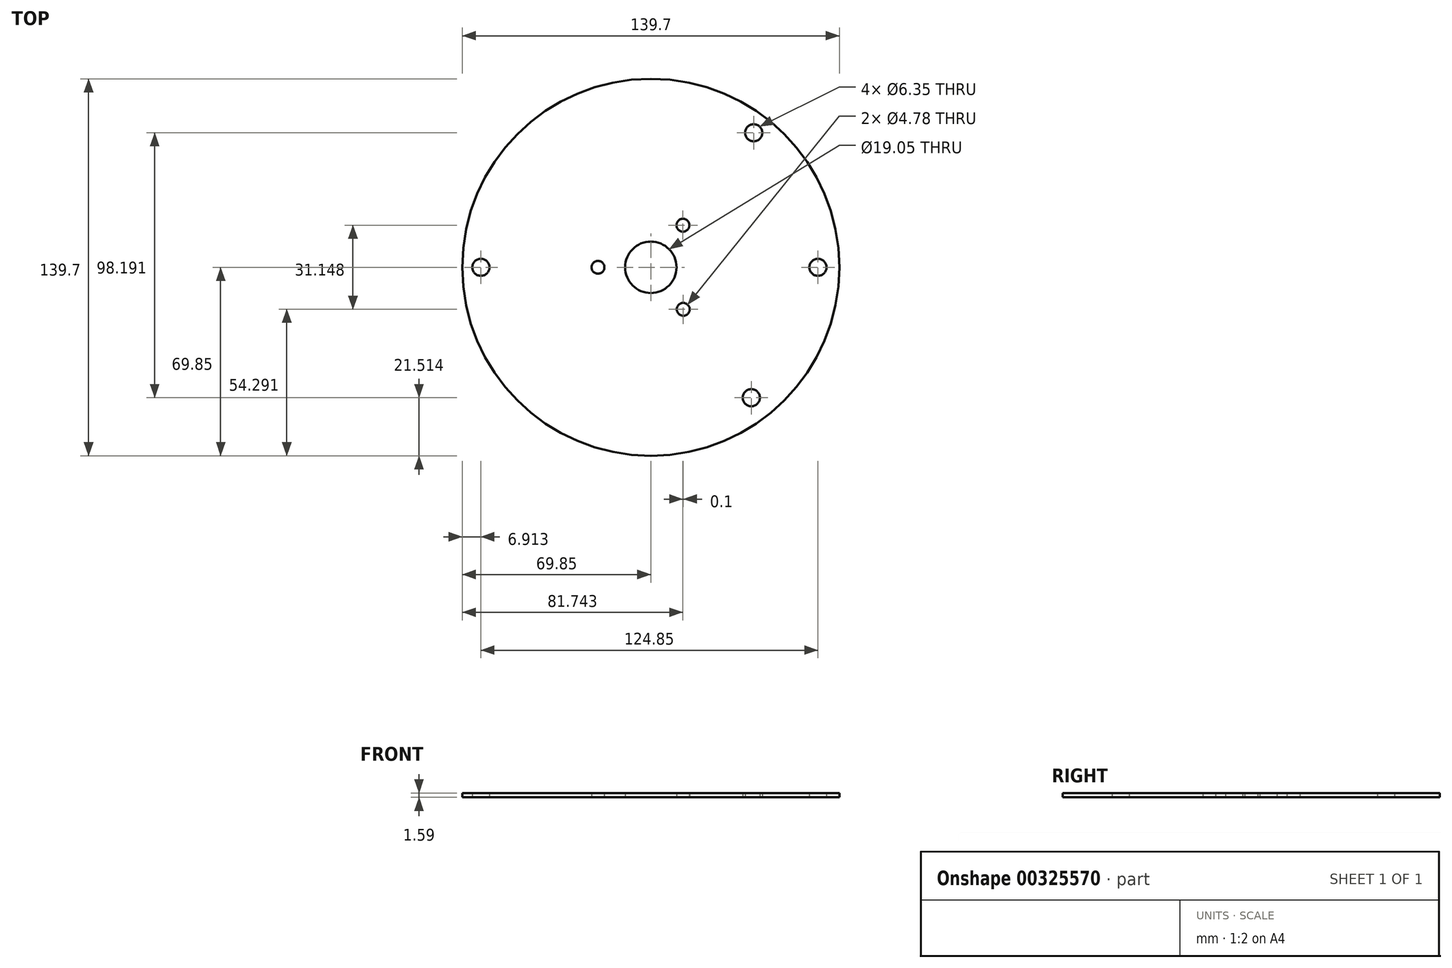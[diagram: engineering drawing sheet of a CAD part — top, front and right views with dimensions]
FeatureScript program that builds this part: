
annotation { "Feature Type Name" : "Feature", "Feature Type Description" : "" }
export const myFeature = defineFeature(function(context is Context, id is Id, definition is map)
    precondition{}
    {
        {
            var Q0;
            Q0=qCreatedBy(makeId("Top.planeOp"),FACE);
            var sketch = newSketch(context, id + "F0", { "sketchPlane" : qUnion([Q0])});
            skPoint(sketch, "E0.start.orphan", {"position": v(0, -587.38) * mm});
            skLineSegment(sketch, "E1", {"start": v(0, 0) * mm, "end": v(-102.34, 0) * mm, "construction": true});
            skLineSegment(sketch, "E2", {"start": v(0, 0) * mm, "end": v(180.46, 0) * mm, "construction": true});
            skLineSegment(sketch, "E3", {"start": v(0, -149.74) * mm, "end": v(0, 151.2) * mm, "construction": true});
            skCircle(sketch, "E4", {"center": v(0, 0) * mm, "radius": 9.53 * mm});
            skCircle(sketch, "E5", {"center": v(-19.56, 0) * mm, "radius": 2.38 * mm});
            skCircle(sketch, "E6", {"center": v(0, 0) * mm, "radius": 17.22 * mm});
            skCircle(sketch, "E7", {"center": v(11.9, 15.59) * mm, "radius": 2.39 * mm});
            skCircle(sketch, "E8", {"center": v(12, -15.56) * mm, "radius": 2.39 * mm});
            skLineSegment(sketch, "E9", {"start": v(9.53, 0) * mm, "end": v(9.53, 25.1) * mm, "construction": true});
            skLineSegment(sketch, "E10", {"start": v(9.53, 0) * mm, "end": v(9.53, -24.17) * mm, "construction": true});
            skCircle(sketch, "E11", {"center": v(61.91, 0) * mm, "radius": 3.18 * mm});
            skCircle(sketch, "E12", {"center": v(0, 0) * mm, "radius": 69.85 * mm});
            skCircle(sketch, "E13", {"center": v(-62.94, 0) * mm, "radius": 3.18 * mm});
            skLineSegment(sketch, "E14", {"start": v(0, 0) * mm, "end": v(55.59, -72.2) * mm, "construction": true});
            skLineSegment(sketch, "E15", {"start": v(0, 0) * mm, "end": v(50.13, 65.58) * mm, "construction": true});
            skCircle(sketch, "E16", {"center": v(38.1, 49.85) * mm, "radius": 3.18 * mm});
            skCircle(sketch, "E17", {"center": v(37.22, -48.34) * mm, "radius": 3.18 * mm});
            skSolve(sketch);
        }
        {
            var Q0;
            Q0=makeQuery(id+"F0.imprint","IMPRINT",FACE,{"disambiguationData":[TD([[makeQuery(id+"F0.imprint","IMPRINT",EDGE,{"derivedFrom":sQuery(id+"F0.wireOp",EDGE,"E4")}),-1.0]])]});
            var Q1;
            Q1=makeQuery(id+"F0.imprint","IMPRINT",FACE,{"disambiguationData":[TD([[makeQuery(id+"F0.imprint","IMPRINT",EDGE,{"derivedFrom":sQuery(id+"F0.wireOp",EDGE,"E8")}),-1.0]])]});
            extrude(context, id + "F1", {"entities" : qUnion([Q0, Q1]), "depth" : 1.59 * mm});
        }
    });
